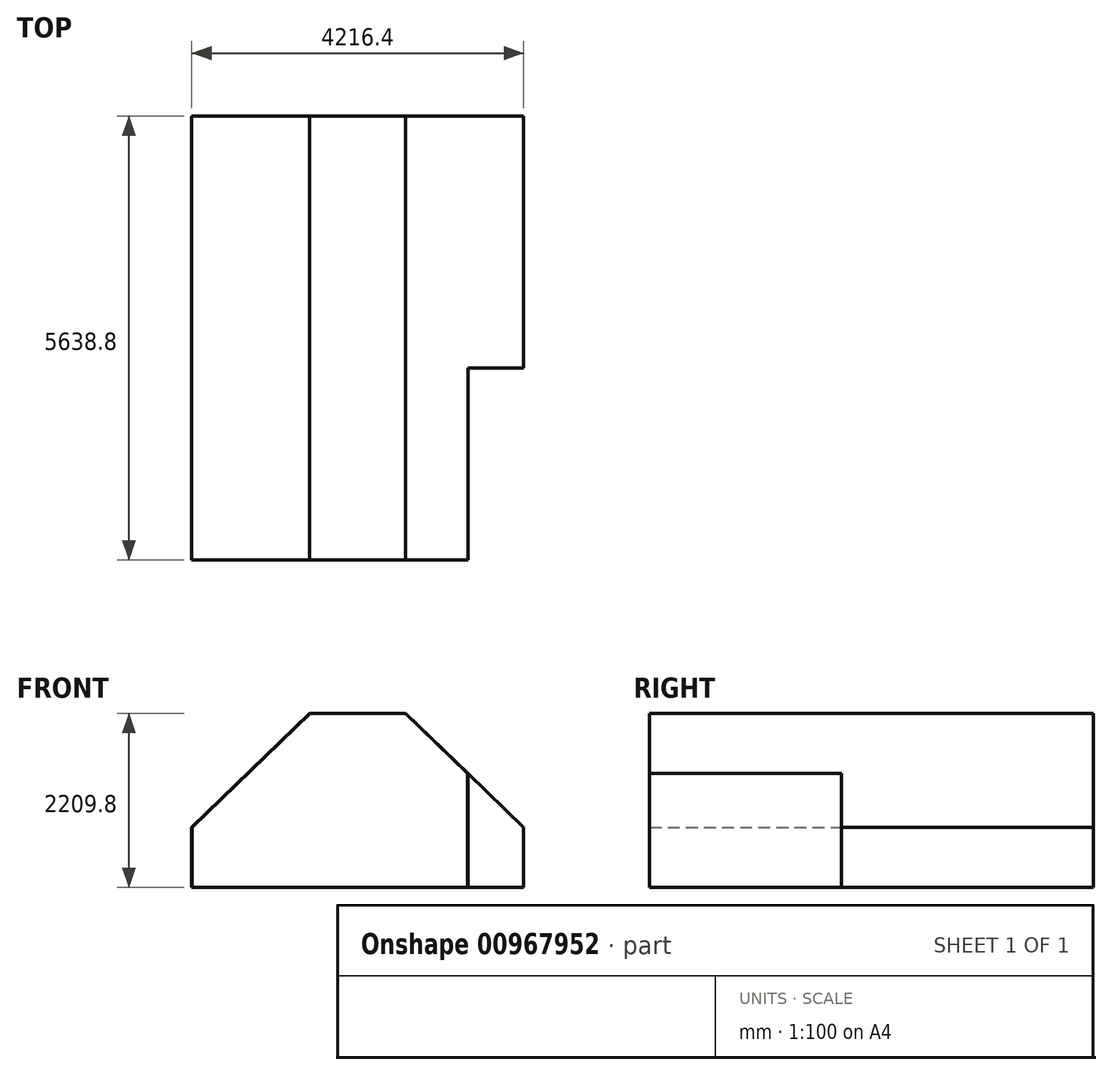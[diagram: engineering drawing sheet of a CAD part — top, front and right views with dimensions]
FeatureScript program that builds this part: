
annotation { "Feature Type Name" : "Feature", "Feature Type Description" : "" }
export const myFeature = defineFeature(function(context is Context, id is Id, definition is map)
    precondition{}
    {
        {
            var Q0;
            Q0=qCreatedBy(makeId("Front.planeOp"),FACE);
            var sketch = newSketch(context, id + "F0", { "sketchPlane" : qUnion([Q0])});
            skLineSegment(sketch, "E0", {"start": v(0, 0) * mm, "end": v(0, 762) * mm});
            skLineSegment(sketch, "E1", {"start": v(0, 762) * mm, "end": v(1498.6, 2209.8) * mm});
            skLineSegment(sketch, "E2", {"start": v(1498.6, 2209.8) * mm, "end": v(2717.8, 2209.8) * mm});
            skLineSegment(sketch, "E3", {"start": v(2717.8, 2209.8) * mm, "end": v(4216.4, 762) * mm});
            skLineSegment(sketch, "E4", {"start": v(4216.4, 762) * mm, "end": v(4216.4, 0) * mm});
            skLineSegment(sketch, "E5", {"start": v(4216.4, 0) * mm, "end": v(0, 0) * mm});
            skSolve(sketch);
        }
        {
            var Q0;
            Q0=makeQuery(id+"F0.imprint","IMPRINT",FACE,{"disambiguationData":[TD([[makeQuery(id+"F0.imprint","IMPRINT",EDGE,{"derivedFrom":sQuery(id+"F0.wireOp",EDGE,"E0")}),-1.0]])]});
            extrude(context, id + "F1", {"entities" : qUnion([Q0]), "depth" : 3200.4 * mm, "offsetDistance" : 25.4 * mm});
        }
        {
            var Q0;
            Q0=makeQuery(id+"F1.opExtrude","CAP_FACE",FACE,{"disambiguationData":[OSD([sQuery(id+"F0.wireOp",EDGE,"E0"),sQuery(id+"F0.wireOp",EDGE,"E1"),sQuery(id+"F0.wireOp",EDGE,"E2"),sQuery(id+"F0.wireOp",EDGE,"E3"),sQuery(id+"F0.wireOp",EDGE,"E4"),sQuery(id+"F0.wireOp",EDGE,"E5")])],"isStart":false});
            var sketch = newSketch(context, id + "F2", { "sketchPlane" : qUnion([Q0])});
            skLineSegment(sketch, "E6.0.0", {"start": v(0, 0) * mm, "end": v(4216.4, 0) * mm});
            skLineSegment(sketch, "E6.0.1", {"start": v(4216.4, 0) * mm, "end": v(4216.4, 762) * mm});
            skLineSegment(sketch, "E6.0.2", {"start": v(4216.4, 762) * mm, "end": v(2717.8, 2209.8) * mm});
            skLineSegment(sketch, "E6.0.3", {"start": v(2717.8, 2209.8) * mm, "end": v(1498.6, 2209.8) * mm});
            skLineSegment(sketch, "E6.0.4", {"start": v(1498.6, 2209.8) * mm, "end": v(0, 762) * mm});
            skLineSegment(sketch, "E6.0.5", {"start": v(0, 762) * mm, "end": v(0, 0) * mm});
            skLineSegment(sketch, "E7", {"start": v(3506.54, 1447.8) * mm, "end": v(3506.54, 0) * mm});
            skSolve(sketch);
        }
        {
            var Q0;
            {var subQ0=sQuery(id+"F2.wireOp",EDGE,"E6.0.3");Q0=makeQuery(id+"F2.imprint","IMPRINT",FACE,{"disambiguationData":[TD([[makeQuery(id+"F2.imprint","IMPRINT",EDGE,{"derivedFrom":subQ0}),-1.0]])]});}
            extrude(context, id + "F3", {"entities" : qUnion([Q0]), "operationType" : NewBodyOperationType.ADD, "depth" : 2438.4 * mm, "offsetDistance" : 25.4 * mm});
        }
        {
            var Q0;
            Q0=makeQuery(id+"F1.opExtrude","CAP_FACE",FACE,{"disambiguationData":[OSD([sQuery(id+"F0.wireOp",EDGE,"E0"),sQuery(id+"F0.wireOp",EDGE,"E1"),sQuery(id+"F0.wireOp",EDGE,"E2"),sQuery(id+"F0.wireOp",EDGE,"E3"),sQuery(id+"F0.wireOp",EDGE,"E4"),sQuery(id+"F0.wireOp",EDGE,"E5")])],"isStart":true});
            var Q1;
            Q1=makeQuery(id+"F3.opExtrude","CAP_FACE",FACE,{"disambiguationData":[OSD([sQuery(id+"F2.wireOp",EDGE,"E6.0.0"),sQuery(id+"F2.wireOp",EDGE,"E6.0.2"),sQuery(id+"F2.wireOp",EDGE,"E6.0.3"),sQuery(id+"F2.wireOp",EDGE,"E6.0.4"),sQuery(id+"F2.wireOp",EDGE,"E6.0.5"),sQuery(id+"F2.wireOp",EDGE,"E7")])],"isStart":false});
            shell(context, id + "F4", {"entities" : qUnion([Q0, Q1]), "thickness" : 2.54 * mm});
        }
    });
